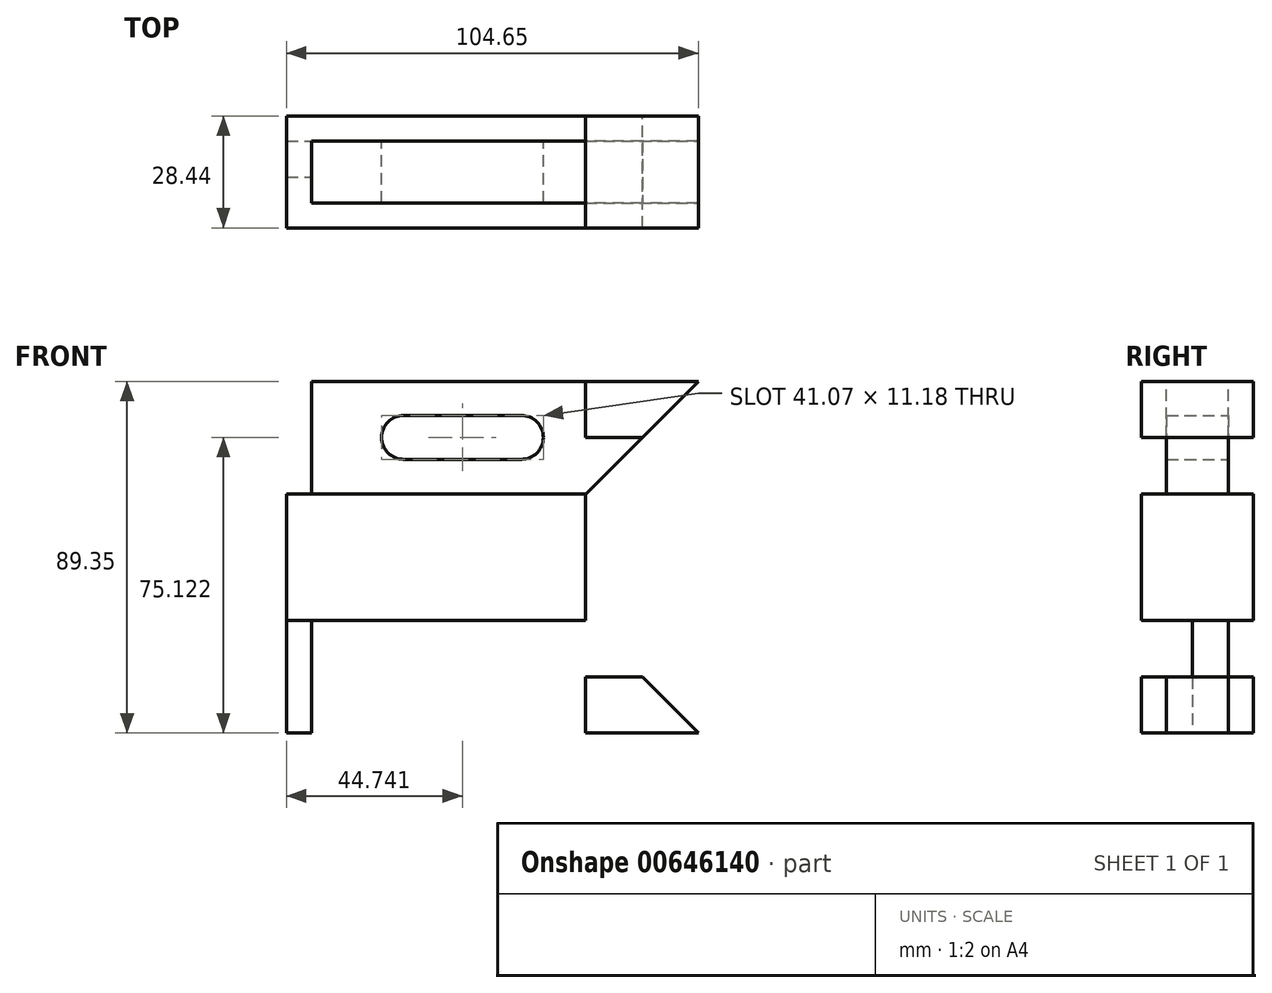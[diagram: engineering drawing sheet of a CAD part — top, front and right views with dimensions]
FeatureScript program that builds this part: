
annotation { "Feature Type Name" : "Feature", "Feature Type Description" : "" }
export const myFeature = defineFeature(function(context is Context, id is Id, definition is map)
    precondition{}
    {
        {
            var Q0;
            Q0=qCreatedBy(makeId("Front.planeOp"),FACE);
            var sketch = newSketch(context, id + "F0", { "sketchPlane" : qUnion([Q0])});
            skLineSegment(sketch, "E0", {"start": v(-37.3, 66.28) * mm, "end": v(67.34, 66.28) * mm});
            skLineSegment(sketch, "E1", {"start": v(-37.3, -23.07) * mm, "end": v(67.34, -23.07) * mm});
            skLineSegment(sketch, "E2", {"start": v(-37.3, 66.28) * mm, "end": v(-37.3, -23.07) * mm});
            skLineSegment(sketch, "E3.0", {"start": v(-37.3, 5.5) * mm, "end": v(69.8, 5.5) * mm});
            skLineSegment(sketch, "E4.0", {"start": v(-37.3, 37.7) * mm, "end": v(67.34, 37.7) * mm});
            skLineSegment(sketch, "E5", {"start": v(67.34, -23.07) * mm, "end": v(38.76, 5.5) * mm});
            skLineSegment(sketch, "E6", {"start": v(-37.3, 21.6) * mm, "end": v(85.31, 21.6) * mm});
            skLineSegment(sketch, "E7", {"start": v(-37.3, 66.28) * mm, "end": v(-30.96, 66.28) * mm});
            skLineSegment(sketch, "E8", {"start": v(-30.96, 66.28) * mm, "end": v(-30.96, -23.07) * mm});
            skLineSegment(sketch, "E9", {"start": v(-30.96, 5.5) * mm, "end": v(38.64, 5.5) * mm});
            skLineSegment(sketch, "E10", {"start": v(38.64, -8.84) * mm, "end": v(38.64, -23.07) * mm});
            skLineSegment(sketch, "E11", {"start": v(-37.3, -23.07) * mm, "end": v(-37.3, -8.84) * mm});
            skArc(sketch, "E12", {"start": v(-7.52, -3.25) * mm, "mid": v(-13.1, -8.84) * mm, "end": v(-7.52, -14.43) * mm});
            skArc(sketch, "E13", {"start": v(22.38, -14.43) * mm, "mid": v(27.97, -8.84) * mm, "end": v(22.38, -3.25) * mm});
            skLineSegment(sketch, "E14", {"start": v(-7.52, -3.25) * mm, "end": v(22.38, -3.25) * mm});
            skLineSegment(sketch, "E15", {"start": v(-7.52, -14.43) * mm, "end": v(22.38, -14.43) * mm});
            skLineSegment(sketch, "E16.trimOffspring", {"start": v(-13.1, -8.84) * mm, "end": v(-12.67, -8.84) * mm});
            skLineSegment(sketch, "E17.trimOffspring", {"start": v(38.64, -8.84) * mm, "end": v(53.11, -8.84) * mm});
            skLineSegment(sketch, "E18", {"start": v(38.64, 5.5) * mm, "end": v(38.64, 21.6) * mm});
            skLineSegment(sketch, "E19.MirrorCS", {"start": v(-13.1, 52.05) * mm, "end": v(-12.67, 52.05) * mm});
            skArc(sketch, "E20.MirrorCS", {"start": v(-7.52, 46.46) * mm, "mid": v(-13.1, 52.05) * mm, "end": v(-7.52, 57.64) * mm});
            skLineSegment(sketch, "E21.MirrorCS", {"start": v(38.64, 52.05) * mm, "end": v(38.64, 66.28) * mm});
            skLineSegment(sketch, "E22.MirrorCS", {"start": v(-30.96, 37.7) * mm, "end": v(38.64, 37.7) * mm});
            skLineSegment(sketch, "E23.MirrorCS", {"start": v(38.64, 37.7) * mm, "end": v(38.64, 21.6) * mm});
            skLineSegment(sketch, "E24.MirrorCS", {"start": v(-7.52, 46.46) * mm, "end": v(22.38, 46.46) * mm});
            skLineSegment(sketch, "E25.MirrorCS", {"start": v(-7.52, 57.64) * mm, "end": v(22.38, 57.64) * mm});
            skLineSegment(sketch, "E26.MirrorCS", {"start": v(-30.96, -23.07) * mm, "end": v(-30.96, 66.28) * mm});
            skLineSegment(sketch, "E27.MirrorCS", {"start": v(38.64, 52.05) * mm, "end": v(53.11, 52.05) * mm});
            skLineSegment(sketch, "E28.MirrorCS", {"start": v(67.34, 66.28) * mm, "end": v(38.76, 37.7) * mm});
            skLineSegment(sketch, "E29.MirrorCS", {"start": v(-37.3, 37.7) * mm, "end": v(69.8, 37.7) * mm});
            skArc(sketch, "E30.MirrorCS", {"start": v(22.38, 57.64) * mm, "mid": v(27.97, 52.05) * mm, "end": v(22.38, 46.46) * mm});
            skLineSegment(sketch, "E31.MirrorCS", {"start": v(-37.3, -23.07) * mm, "end": v(-37.3, 66.28) * mm});
            skLineSegment(sketch, "E32.MirrorCS", {"start": v(-37.3, 66.28) * mm, "end": v(-37.3, 52.05) * mm});
            skSolve(sketch);
        }
        {
            var Q0;
            {var subQ8=sQuery(id+"F0.wireOp",EDGE,"E9");Q0=makeQuery(id+"F0.imprint","IMPRINT",FACE,{"disambiguationData":[TD([[makeQuery(id+"F0.imprint","IMPRINT",EDGE,{"derivedFrom":subQ8}),-1.0]])]});}
            var Q1;
            {var subQ11=sQuery(id+"F0.wireOp",EDGE,"E21.MirrorCS");Q1=makeQuery(id+"F0.imprint","IMPRINT",FACE,{"disambiguationData":[TD([[makeQuery(id+"F0.imprint","IMPRINT",EDGE,{"derivedFrom":subQ11}),1.0]])]});}
            extrude(context, id + "F1", {"entities" : qUnion([Q0, Q1]), "endBound" : BoundingType.SYMMETRIC, "depth" : 15.75 * mm, "offsetDistance" : 25.4 * mm});
        }
        {
            var Q0;
            {var subQ3=sQuery(id+"F0.wireOp",EDGE,"E10");Q0=makeQuery(id+"F0.imprint","IMPRINT",FACE,{"disambiguationData":[TD([[makeQuery(id+"F0.imprint","IMPRINT",EDGE,{"derivedFrom":subQ3}),1.0]])]});}
            var Q1;
            {var subQ0=sQuery(id+"F0.wireOp",EDGE,"E31.MirrorCS");var subQ5=sQuery(id+"F0.wireOp",EDGE,"E6");var subQ6=makeQuery(id+"F0.imprint","INTERSECT",VERTEX,{"derivedFrom":[subQ5,subQ0]});Q1=makeQuery(id+"F0.imprint","IMPRINT",FACE,{"disambiguationData":[TD([[makeQuery(id+"F0.imprint","IMPRINT",EDGE,{"disambiguationData":[TD([[subQ6,-1.0]])],"derivedFrom":subQ5}),-1.0]])]});}
            var Q2;
            {var subQ0=sQuery(id+"F0.wireOp",EDGE,"E21.MirrorCS");Q2=makeQuery(id+"F0.imprint","IMPRINT",FACE,{"disambiguationData":[TD([[makeQuery(id+"F0.imprint","IMPRINT",EDGE,{"derivedFrom":subQ0}),-1.0]])]});}
            var Q3;
            {var subQ4=sQuery(id+"F0.wireOp",EDGE,"E9");Q3=makeQuery(id+"F0.imprint","IMPRINT",FACE,{"disambiguationData":[TD([[makeQuery(id+"F0.imprint","IMPRINT",EDGE,{"derivedFrom":subQ4}),1.0]])]});}
            var Q4;
            {var subQ0=sQuery(id+"F0.wireOp",EDGE,"E23.MirrorCS");Q4=makeQuery(id+"F0.imprint","IMPRINT",FACE,{"disambiguationData":[TD([[makeQuery(id+"F0.imprint","IMPRINT",EDGE,{"derivedFrom":subQ0}),-1.0]])]});}
            var Q5;
            {var subQ0=sQuery(id+"F0.wireOp",EDGE,"E31.MirrorCS");var subQ1=sQuery(id+"F0.wireOp",EDGE,"E6");var subQ2=makeQuery(id+"F0.imprint","INTERSECT",VERTEX,{"derivedFrom":[subQ1,subQ0]});Q5=makeQuery(id+"F0.imprint","IMPRINT",FACE,{"disambiguationData":[TD([[makeQuery(id+"F0.imprint","IMPRINT",EDGE,{"disambiguationData":[TD([[subQ2,-1.0]])],"derivedFrom":subQ1}),1.0]])]});}
            extrude(context, id + "F2", {"entities" : qUnion([Q0, Q1, Q2, Q3, Q4, Q5]), "endBound" : BoundingType.SYMMETRIC, "depth" : 28.45 * mm, "offsetDistance" : 25.4 * mm});
        }
        {
            var Q0;
            {var subQ0=sQuery(id+"F0.wireOp",EDGE,"E32.MirrorCS");Q0=makeQuery(id+"F0.imprint","IMPRINT",FACE,{"disambiguationData":[TD([[makeQuery(id+"F0.imprint","IMPRINT",EDGE,{"derivedFrom":subQ0}),1.0]])]});}
            var Q1;
            {var subQ0=sQuery(id+"F0.wireOp",EDGE,"E31.MirrorCS");var subQ1=sQuery(id+"F0.wireOp",EDGE,"E1");var subQ2=makeQuery(id+"F0.imprint","INTERSECT",VERTEX,{"derivedFrom":[subQ1,subQ0]});Q1=makeQuery(id+"F0.imprint","IMPRINT",FACE,{"disambiguationData":[TD([[makeQuery(id+"F0.imprint","IMPRINT",EDGE,{"disambiguationData":[TD([[subQ2,-1.0]])],"derivedFrom":subQ1}),1.0]])]});}
            extrude(context, id + "F3", {"entities" : qUnion([Q0, Q1]), "endBound" : BoundingType.SYMMETRIC, "oppositeDirection" : true, "depth" : 15.75 * mm, "offsetDistance" : 25.4 * mm});
        }
        {
            var Q0;
            Q0=makeQuery(id+"F3.opExtrude","CAP_FACE",FACE,{"disambiguationData":[OSD([sQuery(id+"F0.wireOp",EDGE,"E1"),sQuery(id+"F0.wireOp",EDGE,"E3.0"),sQuery(id+"F0.wireOp",EDGE,"E26.MirrorCS"),sQuery(id+"F0.wireOp",EDGE,"E31.MirrorCS")])],"isStart":true});
            var Q1;
            Q1=makeQuery(id+"F3.opExtrude","CAP_FACE",FACE,{"disambiguationData":[OSD([sQuery(id+"F0.wireOp",EDGE,"E26.MirrorCS"),sQuery(id+"F0.wireOp",EDGE,"E29.MirrorCS"),sQuery(id+"F0.wireOp",EDGE,"E31.MirrorCS"),sQuery(id+"F0.wireOp",EDGE,"E32.MirrorCS"),sQuery(id+"F0.wireOp",EDGE,"E0")])],"isStart":true});
            extrude(context, id + "F4", {"entities" : qUnion([Q0, Q1]), "operationType" : NewBodyOperationType.REMOVE, "oppositeDirection" : true, "depth" : 6.6 * mm, "offsetDistance" : 25.4 * mm});
        }
    });
